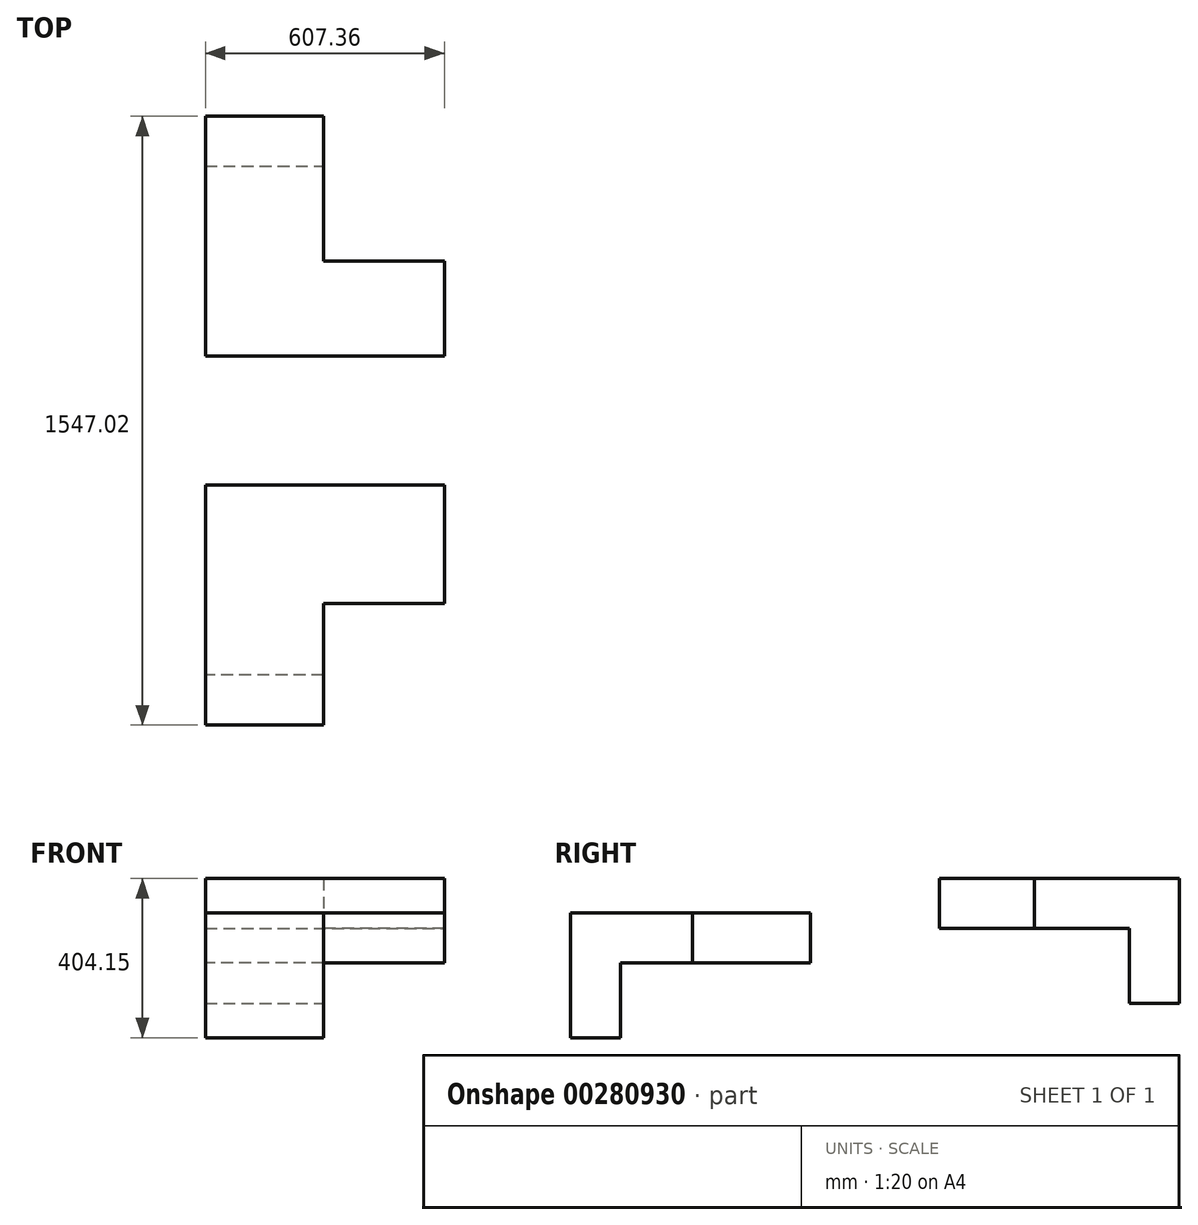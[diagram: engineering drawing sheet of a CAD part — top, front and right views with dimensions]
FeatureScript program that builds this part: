
annotation { "Feature Type Name" : "Feature", "Feature Type Description" : "" }
export const myFeature = defineFeature(function(context is Context, id is Id, definition is map)
    precondition{}
    {
        {
            var Q0;
            Q0=qCreatedBy(makeId("Top.planeOp"),FACE);
            var sketch = newSketch(context, id + "F0", { "sketchPlane" : qUnion([Q0])});
            skLineSegment(sketch, "E0.bottom", {"start": v(0, 0) * mm, "end": v(300.3, 0) * mm});
            skLineSegment(sketch, "E0.top", {"start": v(0, 127) * mm, "end": v(300.3, 127) * mm});
            skLineSegment(sketch, "E0.left", {"start": v(0, 0) * mm, "end": v(0, 127) * mm});
            skLineSegment(sketch, "E0.right", {"start": v(300.3, 0) * mm, "end": v(300.3, 127) * mm});
            skSolve(sketch);
        }
        {
            var Q0;
            Q0=makeQuery(id+"F0.imprint","IMPRINT",FACE,{"disambiguationData":[TD([[makeQuery(id+"F0.imprint","IMPRINT",EDGE,{"derivedFrom":sQuery(id+"F0.wireOp",EDGE,"E0.bottom")}),1.0]])]});
            extrude(context, id + "F1", {"entities" : qUnion([Q0]), "depth" : 404.15 * mm, "offsetDistance" : 25.4 * mm});
        }
        {
            var Q0;
            Q0=makeQuery(id+"F1.opExtrude","SWEPT_FACE",FACE,{"disambiguationData":[OSD([sQuery(id+"F0.wireOp",EDGE,"E0.bottom")])]});
            var sketch = newSketch(context, id + "F2", { "sketchPlane" : qUnion([Q0])});
            skLineSegment(sketch, "E1.bottom", {"start": v(0, 404.15) * mm, "end": v(300.3, 404.15) * mm});
            skLineSegment(sketch, "E1.top", {"start": v(0, 277.15) * mm, "end": v(300.3, 277.15) * mm});
            skLineSegment(sketch, "E1.left", {"start": v(0, 404.15) * mm, "end": v(0, 277.15) * mm});
            skLineSegment(sketch, "E1.right", {"start": v(300.3, 404.15) * mm, "end": v(300.3, 277.15) * mm});
            skSolve(sketch);
        }
        {
            var Q0;
            Q0=makeQuery(id+"F2.imprint","IMPRINT",FACE,{"disambiguationData":[TD([[makeQuery(id+"F2.imprint","IMPRINT",EDGE,{"derivedFrom":sQuery(id+"F2.wireOp",EDGE,"E1.bottom")}),-1.0]])]});
            extrude(context, id + "F3", {"entities" : qUnion([Q0]), "operationType" : NewBodyOperationType.ADD, "depth" : 396.24 * mm, "offsetDistance" : 25.4 * mm});
        }
        {
            var Q0;
            Q0=makeQuery(id+"F3.opExtrude","CAP_FACE",FACE,{"disambiguationData":[OSD([sQuery(id+"F2.wireOp",EDGE,"E1.bottom"),sQuery(id+"F2.wireOp",EDGE,"E1.top"),sQuery(id+"F2.wireOp",EDGE,"E1.left"),sQuery(id+"F2.wireOp",EDGE,"E1.right")])],"isStart":false});
            extrude(context, id + "F4", {"entities" : qUnion([Q0]), "operationType" : NewBodyOperationType.ADD, "depth" : 86.65 * mm, "offsetDistance" : 25.4 * mm});
        }
        {
            var Q0;
            {var subQ0=sQuery(id+"F2.wireOp",EDGE,"E1.right");Q0=makeQuery(id+"F4.boolean.opBoolean","MERGE",FACE,{"derivedFrom":[makeQuery(id+"F3.boolean.opBoolean","MERGE",FACE,{"derivedFrom":[makeQuery(id+"F1.opExtrude","SWEPT_FACE",FACE,{"disambiguationData":[OSD([sQuery(id+"F0.wireOp",EDGE,"E0.right")])]}),makeQuery(id+"F3.opExtrude","SWEPT_FACE",FACE,{"disambiguationData":[OSD([subQ0])]})]}),makeQuery(id+"F4.opExtrude","SWEPT_FACE",FACE,{"disambiguationData":[OSD([subQ0])]})]});}
            var sketch = newSketch(context, id + "F5", { "sketchPlane" : qUnion([Q0])});
            skLineSegment(sketch, "E2.bottom", {"start": v(-482.9, 404.15) * mm, "end": v(-241.45, 404.15) * mm});
            skLineSegment(sketch, "E2.top", {"start": v(-482.9, 277.15) * mm, "end": v(-241.45, 277.15) * mm});
            skLineSegment(sketch, "E2.left", {"start": v(-482.9, 404.15) * mm, "end": v(-482.9, 277.15) * mm});
            skLineSegment(sketch, "E2.right", {"start": v(-241.45, 404.15) * mm, "end": v(-241.45, 277.15) * mm});
            skSolve(sketch);
        }
        {
            var Q0;
            Q0=makeQuery(id+"F5.imprint","IMPRINT",FACE,{"disambiguationData":[TD([[makeQuery(id+"F5.imprint","IMPRINT",EDGE,{"derivedFrom":sQuery(id+"F5.wireOp",EDGE,"E2.bottom")}),-1.0]])]});
            extrude(context, id + "F6", {"entities" : qUnion([Q0]), "operationType" : NewBodyOperationType.ADD, "depth" : 307.05 * mm, "offsetDistance" : 25.4 * mm});
        }
        {
            var Q0;
            Q0=makeQuery(id+"F1.opExtrude","CAP_FACE",FACE,{"disambiguationData":[OSD([sQuery(id+"F0.wireOp",EDGE,"E0.bottom"),sQuery(id+"F0.wireOp",EDGE,"E0.top"),sQuery(id+"F0.wireOp",EDGE,"E0.left"),sQuery(id+"F0.wireOp",EDGE,"E0.right")])],"isStart":true});
            extrude(context, id + "F7", {"entities" : qUnion([Q0]), "operationType" : NewBodyOperationType.REMOVE, "oppositeDirection" : true, "depth" : 86.66 * mm, "offsetDistance" : 25.4 * mm});
        }
        {
            var Q0;
            Q0=qCreatedBy(makeId("Top.planeOp"),FACE);
            var sketch = newSketch(context, id + "F8", { "sketchPlane" : qUnion([Q0])});
            skLineSegment(sketch, "E3", {"start": v(0, 0) * mm, "end": v(0, -1420.02) * mm, "construction": true});
            skLineSegment(sketch, "E4.bottom", {"start": v(0, -1420.02) * mm, "end": v(300.3, -1420.02) * mm});
            skLineSegment(sketch, "E4.top", {"start": v(0, -1293.02) * mm, "end": v(300.3, -1293.02) * mm});
            skLineSegment(sketch, "E4.left", {"start": v(0, -1420.02) * mm, "end": v(0, -1293.02) * mm});
            skLineSegment(sketch, "E4.right", {"start": v(300.3, -1420.02) * mm, "end": v(300.3, -1293.02) * mm});
            skSolve(sketch);
        }
        {
            var Q0;
            Q0=makeQuery(id+"F8.imprint","IMPRINT",FACE,{"disambiguationData":[TD([[makeQuery(id+"F8.imprint","IMPRINT",EDGE,{"derivedFrom":sQuery(id+"F8.wireOp",EDGE,"E4.bottom")}),1.0]])]});
            extrude(context, id + "F9", {"entities" : qUnion([Q0]), "depth" : 317.5 * mm, "offsetDistance" : 25.4 * mm});
        }
        {
            var Q0;
            Q0=makeQuery(id+"F9.opExtrude","SWEPT_FACE",FACE,{"disambiguationData":[OSD([sQuery(id+"F8.wireOp",EDGE,"E4.top")])]});
            var sketch = newSketch(context, id + "F10", { "sketchPlane" : qUnion([Q0])});
            skLineSegment(sketch, "E5.bottom", {"start": v(-300.3, 317.5) * mm, "end": v(0, 317.5) * mm});
            skLineSegment(sketch, "E5.top", {"start": v(-300.3, 190.5) * mm, "end": v(0, 190.5) * mm});
            skLineSegment(sketch, "E5.left", {"start": v(-300.3, 317.5) * mm, "end": v(-300.3, 190.5) * mm});
            skLineSegment(sketch, "E5.right", {"start": v(0, 317.5) * mm, "end": v(0, 190.5) * mm});
            skSolve(sketch);
        }
        {
            var Q0;
            Q0=makeQuery(id+"F10.imprint","IMPRINT",FACE,{"disambiguationData":[TD([[makeQuery(id+"F10.imprint","IMPRINT",EDGE,{"derivedFrom":sQuery(id+"F10.wireOp",EDGE,"E5.bottom")}),1.0]])]});
            extrude(context, id + "F11", {"entities" : qUnion([Q0]), "operationType" : NewBodyOperationType.ADD, "depth" : 482.88 * mm, "offsetDistance" : 25.4 * mm});
        }
        {
            var Q0;
            Q0=makeQuery(id+"F11.boolean.opBoolean","MERGE",FACE,{"derivedFrom":[makeQuery(id+"F9.opExtrude","SWEPT_FACE",FACE,{"disambiguationData":[OSD([sQuery(id+"F8.wireOp",EDGE,"E4.right")])]}),makeQuery(id+"F11.opExtrude","SWEPT_FACE",FACE,{"disambiguationData":[OSD([sQuery(id+"F10.wireOp",EDGE,"E5.left")])]})]});
            var sketch = newSketch(context, id + "F12", { "sketchPlane" : qUnion([Q0])});
            skLineSegment(sketch, "E6.bottom", {"start": v(-810.14, 190.5) * mm, "end": v(-1110.45, 190.5) * mm});
            skLineSegment(sketch, "E6.top", {"start": v(-810.14, 317.5) * mm, "end": v(-1110.45, 317.5) * mm});
            skLineSegment(sketch, "E6.left", {"start": v(-810.14, 190.5) * mm, "end": v(-810.14, 317.5) * mm});
            skLineSegment(sketch, "E6.right", {"start": v(-1110.45, 190.5) * mm, "end": v(-1110.45, 317.5) * mm});
            skSolve(sketch);
        }
        {
            var Q0;
            Q0=makeQuery(id+"F12.imprint","IMPRINT",FACE,{"disambiguationData":[TD([[makeQuery(id+"F12.imprint","IMPRINT",EDGE,{"derivedFrom":sQuery(id+"F12.wireOp",EDGE,"E6.bottom")}),-1.0]])]});
            extrude(context, id + "F13", {"entities" : qUnion([Q0]), "operationType" : NewBodyOperationType.ADD, "depth" : 307.06 * mm, "offsetDistance" : 25.4 * mm});
        }
    });
